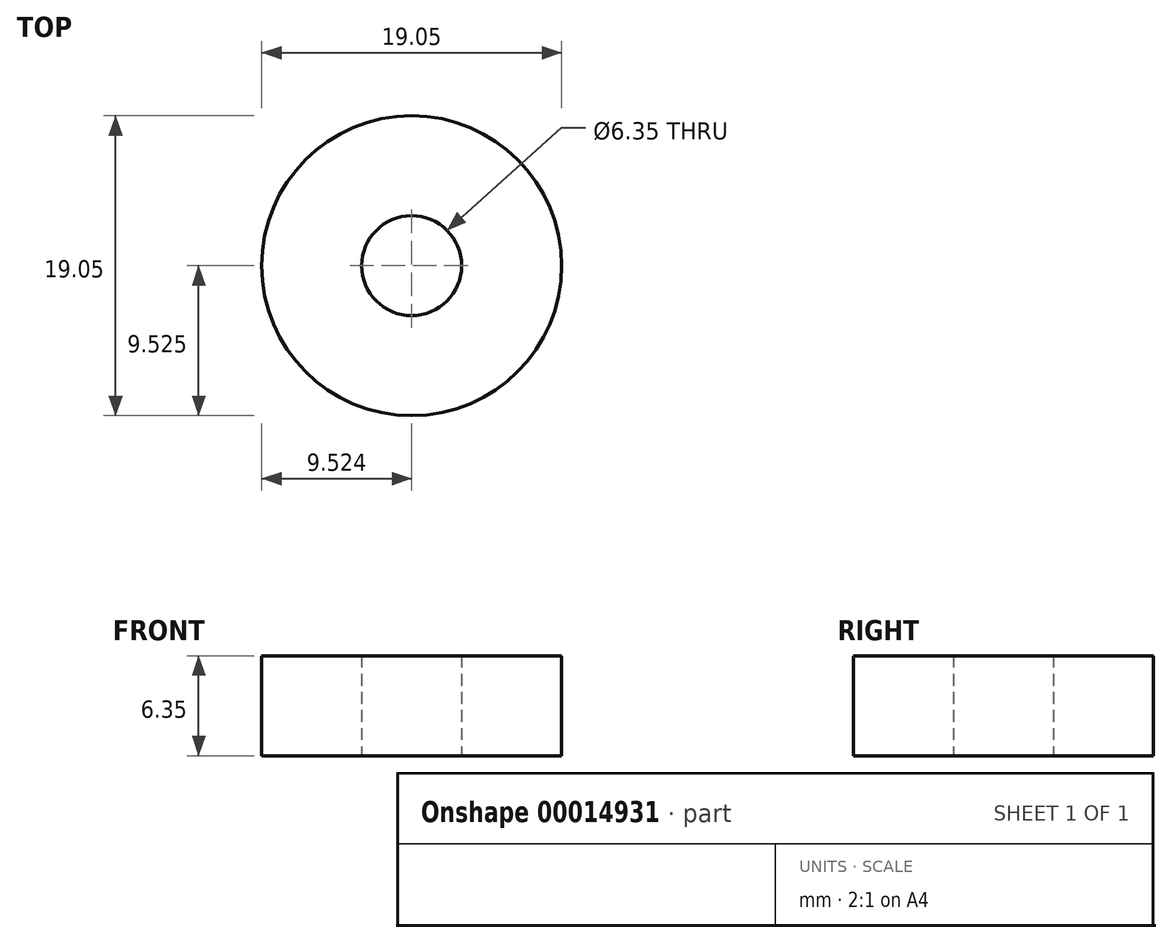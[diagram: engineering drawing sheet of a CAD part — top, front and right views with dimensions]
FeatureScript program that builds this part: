
annotation { "Feature Type Name" : "Feature", "Feature Type Description" : "" }
export const myFeature = defineFeature(function(context is Context, id is Id, definition is map)
    precondition{}
    {
        {
            var Q0;
            Q0=qCreatedBy(makeId("Top.planeOp"),FACE);
            var sketch = newSketch(context, id + "F0", { "sketchPlane" : qUnion([Q0])});
            skCircle(sketch, "E0", {"center": v(-17.8, 29.42) * mm, "radius": 3.18 * mm});
            skCircle(sketch, "E1", {"center": v(-17.8, 29.42) * mm, "radius": 9.53 * mm});
            skSolve(sketch);
        }
        {
            var Q0;
            Q0=makeQuery(id+"F0.imprint","IMPRINT",FACE,{"disambiguationData":[TD([[makeQuery(id+"F0.imprint","IMPRINT",EDGE,{"derivedFrom":sQuery(id+"F0.wireOp",EDGE,"E0")}),-1.0]])]});
            extrude(context, id + "F1", {"entities" : qUnion([Q0]), "depth" : 6.35 * mm});
        }
    });
